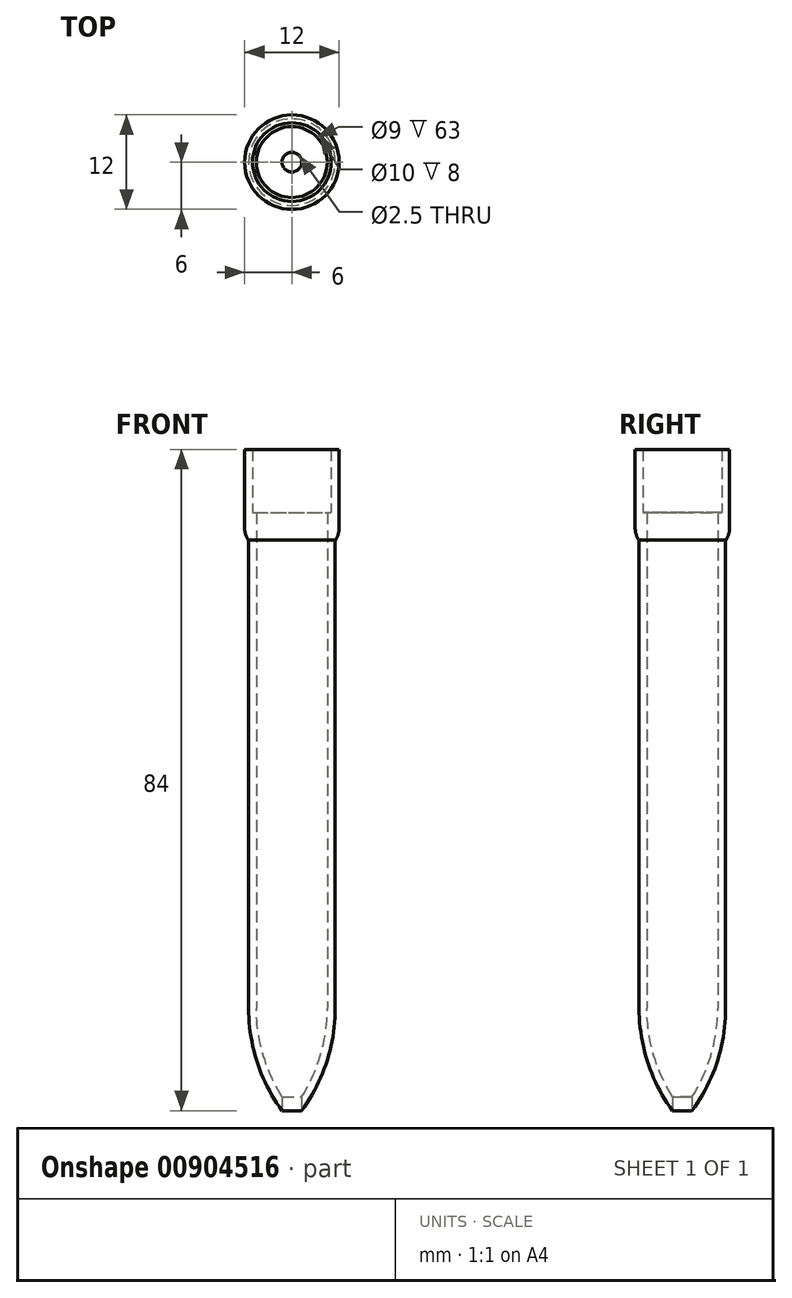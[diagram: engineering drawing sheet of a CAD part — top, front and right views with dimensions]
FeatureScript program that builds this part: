
annotation { "Feature Type Name" : "Feature", "Feature Type Description" : "" }
export const myFeature = defineFeature(function(context is Context, id is Id, definition is map)
    precondition{}
    {
        {
            var Q0;
            Q0=qCreatedBy(makeId("Front.planeOp"),FACE);
            var sketch = newSketch(context, id + "F0", { "sketchPlane" : qUnion([Q0])});
            skLineSegment(sketch, "E0", {"start": v(0, 0) * mm, "end": v(0, 57.97) * mm, "construction": true});
            skLineSegment(sketch, "E1", {"start": v(-4.5, 74.22) * mm, "end": v(-4.5, 11.22) * mm});
            skArc(sketch, "E2", {"start": v(-4.5, 11.22) * mm, "mid": v(-3.67, 5.38) * mm, "end": v(-1.25, 0) * mm});
            skArc(sketch, "E3.0", {"start": v(-5.5, 11.22) * mm, "mid": v(-4.41, 4.39) * mm, "end": v(-1.25, -1.78) * mm});
            skLineSegment(sketch, "E3.1", {"start": v(-5.5, 70.68) * mm, "end": v(-5.5, 11.22) * mm});
            skLineSegment(sketch, "E4", {"start": v(-5, 74.22) * mm, "end": v(-4.5, 74.22) * mm});
            skLineSegment(sketch, "E5", {"start": v(-1.25, 0) * mm, "end": v(-1.25, -1.78) * mm});
            skLineSegment(sketch, "E6.top", {"start": v(-6, 82.22) * mm, "end": v(-5, 82.22) * mm});
            skLineSegment(sketch, "E6.right", {"start": v(-5, 74.22) * mm, "end": v(-5, 82.22) * mm});
            skLineSegment(sketch, "E7", {"start": v(-6, 82.22) * mm, "end": v(-6, 72.22) * mm});
            skArc(sketch, "E8", {"start": v(-6, 72.22) * mm, "mid": v(-5.87, 71.41) * mm, "end": v(-5.5, 70.68) * mm});
            skSolve(sketch);
        }
        {
            var Q0;
            Q0 = qSketchRegion(id + "F0", true);
            var Q1;
            Q1=sQuery(id+"F0.wireOp",EDGE,"E0");
            revolve(context, id + "F1", {"surfaceOperationType" : NewSurfaceOperationType.NEW, "entities" : qUnion([Q0]), "axis" : qUnion([Q1]), "revolveType" : RevolveType.FULL});
        }
    });
